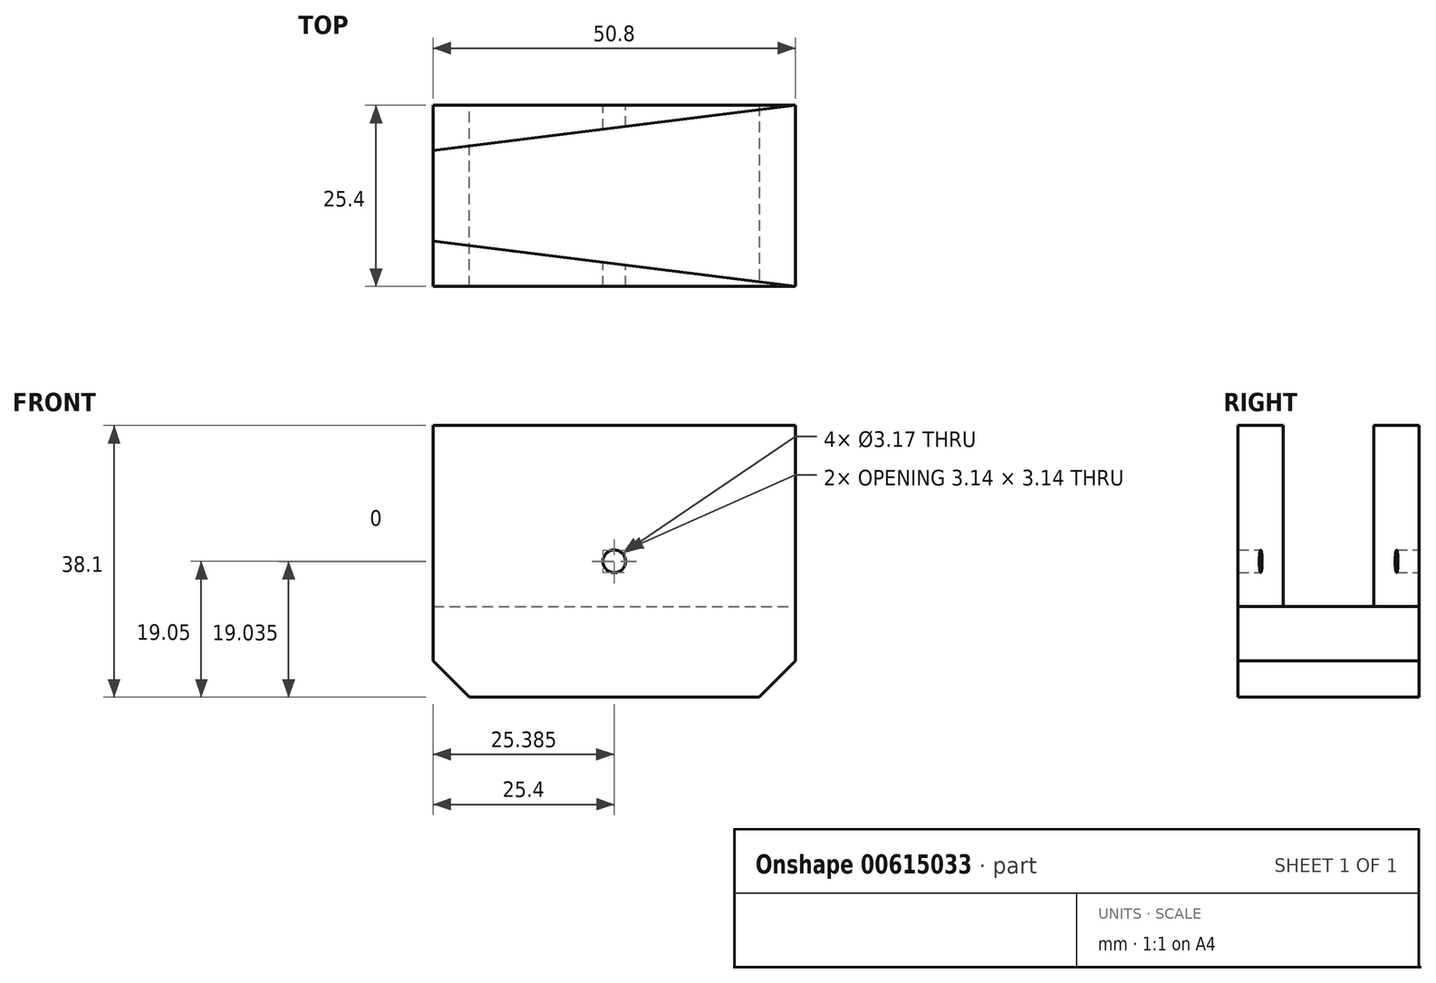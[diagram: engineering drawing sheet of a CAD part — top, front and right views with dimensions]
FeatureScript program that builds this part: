
annotation { "Feature Type Name" : "Feature", "Feature Type Description" : "" }
export const myFeature = defineFeature(function(context is Context, id is Id, definition is map)
    precondition{}
    {
        {
            var Q0;
            Q0=qCreatedBy(makeId("Front.planeOp"),FACE);
            var sketch = newSketch(context, id + "F0", { "sketchPlane" : qUnion([Q0])});
            skLineSegment(sketch, "E0.bottom", {"start": v(0, 0) * mm, "end": v(50.8, 0) * mm});
            skLineSegment(sketch, "E0.top", {"start": v(0, 38.1) * mm, "end": v(50.8, 38.1) * mm});
            skLineSegment(sketch, "E0.left", {"start": v(0, 0) * mm, "end": v(0, 38.1) * mm});
            skLineSegment(sketch, "E0.right", {"start": v(50.8, 0) * mm, "end": v(50.8, 38.1) * mm});
            skLineSegment(sketch, "E1", {"start": v(0, 0) * mm, "end": v(50.8, 38.1) * mm});
            skCircle(sketch, "E2", {"center": v(25.4, 19.05) * mm, "radius": 1.59 * mm});
            skSolve(sketch);
        }
        {
            var Q0;
            Q0 = qSketchRegion(id + "F0", true);
            extrude(context, id + "F1", {"entities" : qUnion([Q0]), "depth" : 25.4 * mm, "offsetDistance" : 25.4 * mm});
        }
        {
            var Q0;
            Q0=makeQuery(id+"F1.opExtrude","SWEPT_FACE",FACE,{"disambiguationData":[OSD([sQuery(id+"F0.wireOp",EDGE,"E0.top")])]});
            var sketch = newSketch(context, id + "F2", { "sketchPlane" : qUnion([Q0])});
            skLineSegment(sketch, "E3", {"start": v(0, -19.05) * mm, "end": v(50.8, -25.4) * mm});
            skLineSegment(sketch, "E4", {"start": v(50.8, 0) * mm, "end": v(0, -6.35) * mm});
            skSolve(sketch);
        }
        {
            var Q0;
            Q0 = qSketchRegion(id + "F2", true);
            var Q1;
            {var subQ0=sQuery(id+"F2.wireOp",EDGE,"E3");Q1=makeQuery(id+"F2.imprint","IMPRINT",FACE,{"disambiguationData":[TD([[makeQuery(id+"F2.imprint","IMPRINT",EDGE,{"derivedFrom":subQ0}),1.0]])]});}
            extrude(context, id + "F3", {"entities" : qUnion([Q0, Q1]), "operationType" : NewBodyOperationType.REMOVE, "oppositeDirection" : true, "depth" : 25.4 * mm, "offsetDistance" : 25.4 * mm});
        }
        {
            var Q0;
            Q0=makeQuery(id+"F1.opExtrude","SWEPT_EDGE",EDGE,{"disambiguationData":[OSD([sQuery(id+"F0.wireOp",EDGE,"E0.bottom"),sQuery(id+"F0.wireOp",EDGE,"E0.right")])]});
            var Q1;
            Q1=makeQuery(id+"F1.opExtrude","SWEPT_EDGE",EDGE,{"disambiguationData":[OSD([sQuery(id+"F0.wireOp",EDGE,"E0.bottom"),sQuery(id+"F0.wireOp",EDGE,"E0.left"),sQuery(id+"F0.wireOp",EDGE,"E1")])]});
            chamfer(context, id + "F4", {"entities" : qUnion([Q0, Q1]), "width" : 5.08 * mm, "tangentPropagation" : true});
        }
    });
